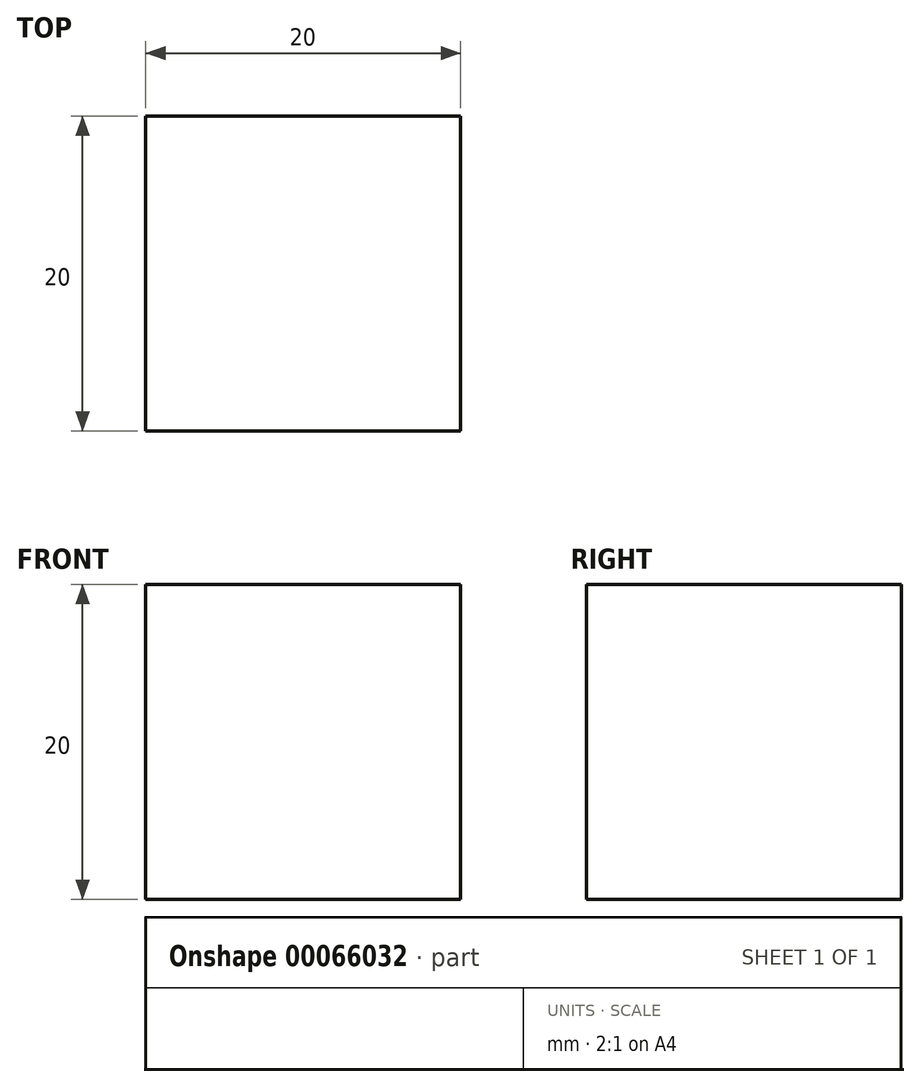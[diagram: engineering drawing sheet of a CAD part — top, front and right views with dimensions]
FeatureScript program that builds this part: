
annotation { "Feature Type Name" : "Feature", "Feature Type Description" : "" }
export const myFeature = defineFeature(function(context is Context, id is Id, definition is map)
    precondition{}
    {
        {
            var Q0;
            Q0=qCreatedBy(makeId("Top.planeOp"),FACE);
            var sketch = newSketch(context, id + "F0", { "sketchPlane" : qUnion([Q0])});
            skLineSegment(sketch, "E0.bottom", {"start": v(0, 0) * mm, "end": v(20, 0) * mm});
            skLineSegment(sketch, "E0.top", {"start": v(0, 20) * mm, "end": v(20, 20) * mm});
            skLineSegment(sketch, "E0.left", {"start": v(0, 0) * mm, "end": v(0, 20) * mm});
            skLineSegment(sketch, "E0.right", {"start": v(20, 0) * mm, "end": v(20, 20) * mm});
            skSolve(sketch);
        }
        {
            var Q0;
            Q0=makeQuery(id+"F0.imprint","IMPRINT",FACE,{"disambiguationData":[TD([[makeQuery(id+"F0.imprint","IMPRINT",EDGE,{"derivedFrom":sQuery(id+"F0.wireOp",EDGE,"E0.bottom")}),1.0]])]});
            extrude(context, id + "F1", {"entities" : qUnion([Q0]), "depth" : 20 * mm});
        }
    });
